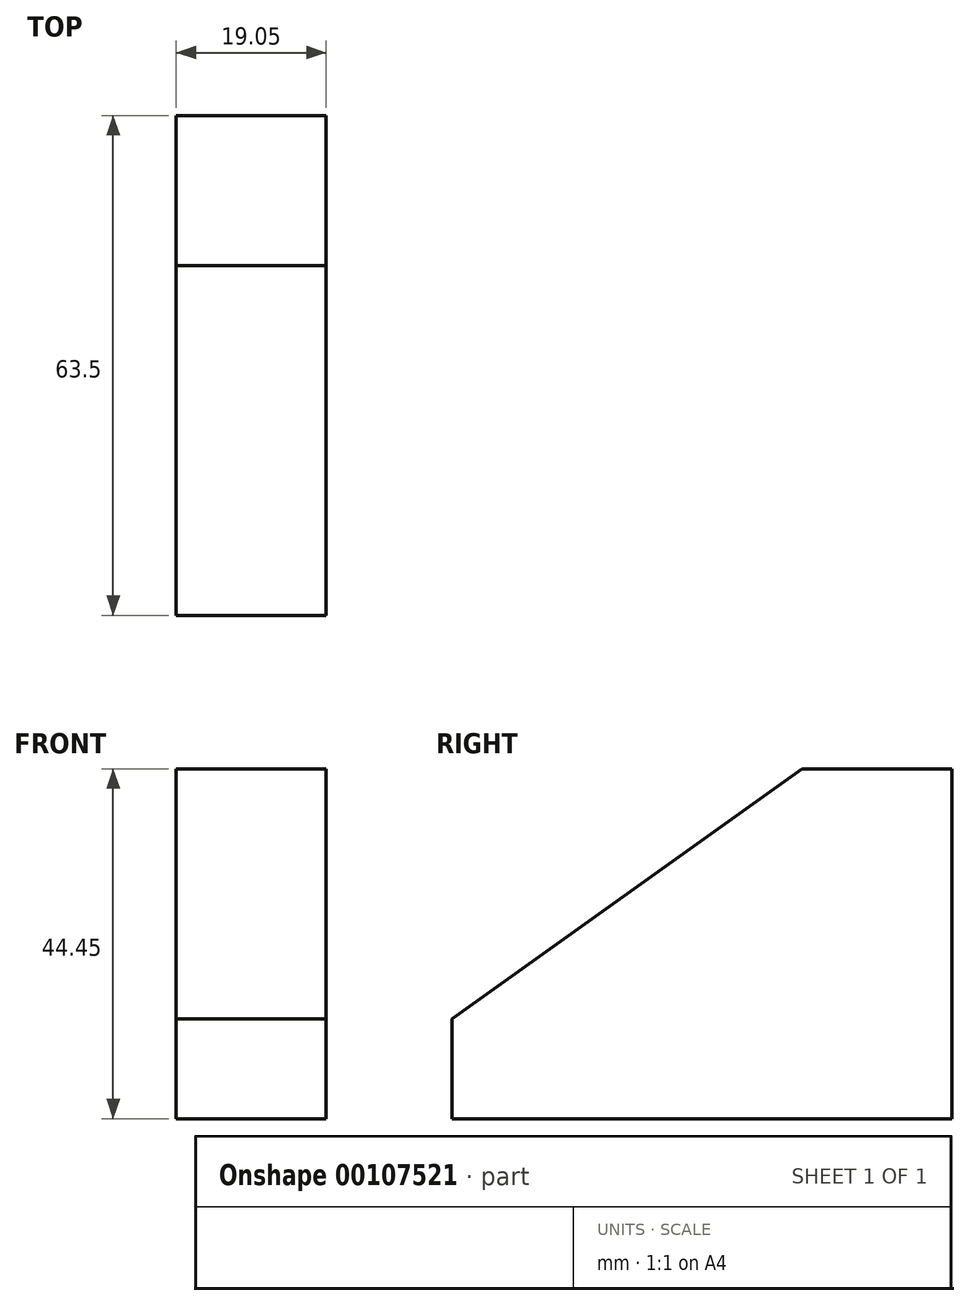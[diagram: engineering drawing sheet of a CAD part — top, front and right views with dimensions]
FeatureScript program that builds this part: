
annotation { "Feature Type Name" : "Feature", "Feature Type Description" : "" }
export const myFeature = defineFeature(function(context is Context, id is Id, definition is map)
    precondition{}
    {
        {
            var Q0;
            Q0=qCreatedBy(makeId("Right.planeOp"),FACE);
            var sketch = newSketch(context, id + "F0", { "sketchPlane" : qUnion([Q0])});
            skLineSegment(sketch, "E0", {"start": v(-12.78, -41.7) * mm, "end": v(50.72, -41.7) * mm});
            skLineSegment(sketch, "E1", {"start": v(50.72, -41.7) * mm, "end": v(50.72, 2.75) * mm});
            skLineSegment(sketch, "E2", {"start": v(50.72, 2.75) * mm, "end": v(31.67, 2.75) * mm});
            skLineSegment(sketch, "E3", {"start": v(-12.78, -41.7) * mm, "end": v(-12.78, -29) * mm});
            skLineSegment(sketch, "E4", {"start": v(-12.78, -29) * mm, "end": v(31.67, 2.75) * mm});
            skSolve(sketch);
        }
        {
            var Q0;
            Q0=makeQuery(id+"F0.imprint","IMPRINT",FACE,{"disambiguationData":[TD([[makeQuery(id+"F0.imprint","IMPRINT",EDGE,{"derivedFrom":sQuery(id+"F0.wireOp",EDGE,"E0")}),1.0]])]});
            extrude(context, id + "F1", {"entities" : qUnion([Q0]), "depth" : 19.05 * mm});
        }
    });
